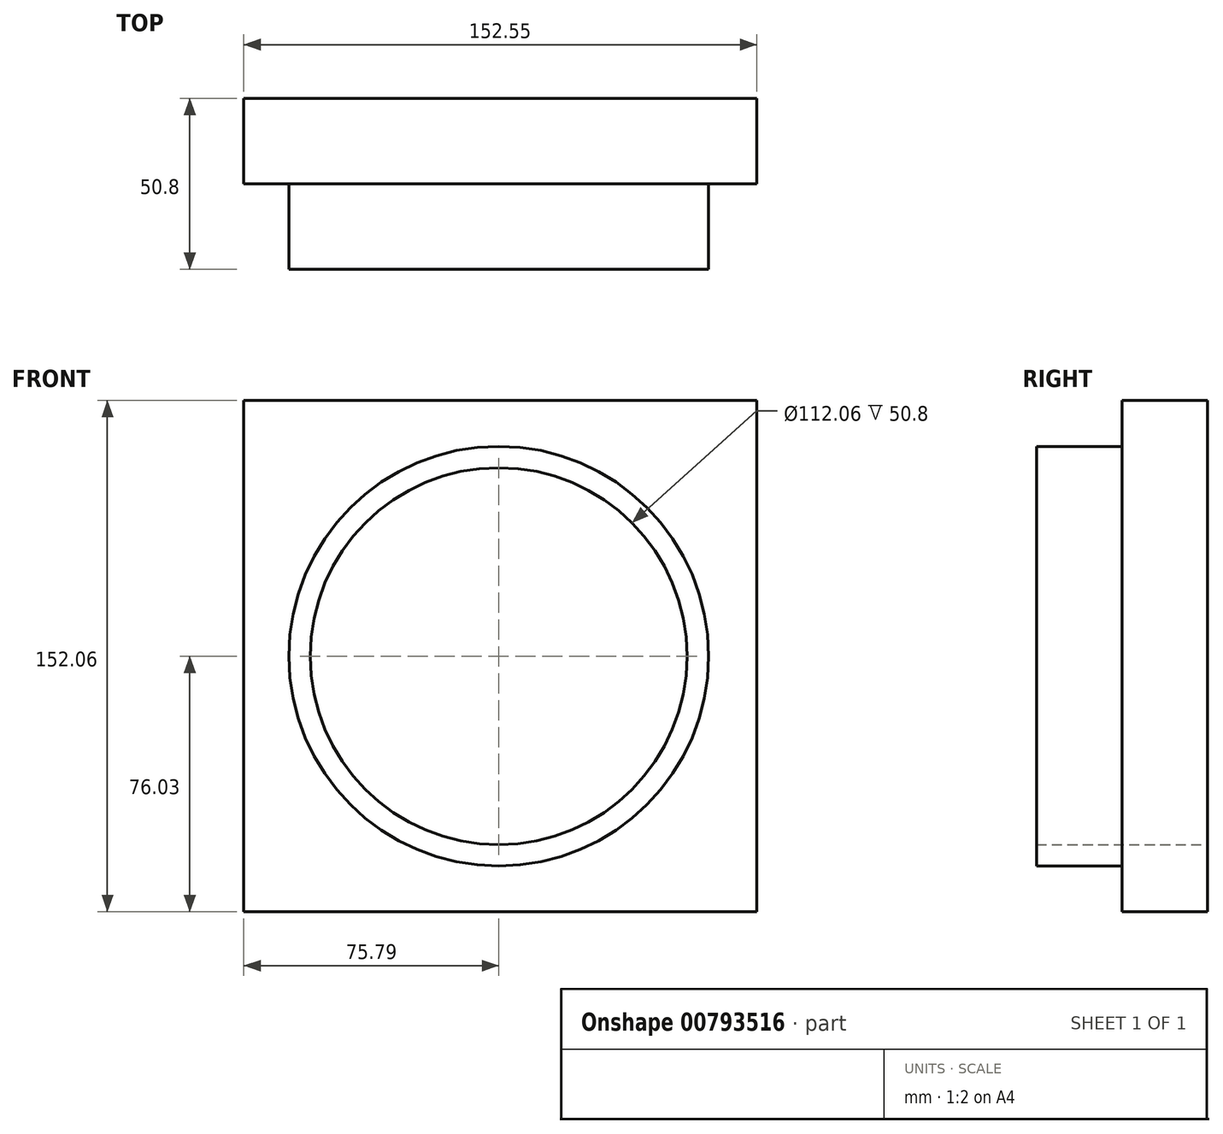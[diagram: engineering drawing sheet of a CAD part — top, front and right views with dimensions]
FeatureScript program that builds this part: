
annotation { "Feature Type Name" : "Feature", "Feature Type Description" : "" }
export const myFeature = defineFeature(function(context is Context, id is Id, definition is map)
    precondition{}
    {
        {
            var Q0;
            Q0=qCreatedBy(makeId("Front.planeOp"),FACE);
            var sketch = newSketch(context, id + "F0", { "sketchPlane" : qUnion([Q0])});
            skCircle(sketch, "E0", {"center": v(0, 0) * mm, "radius": 56.03 * mm});
            skLineSegment(sketch, "E1.bottom", {"start": v(-75.8, 76.03) * mm, "end": v(76.76, 76.03) * mm});
            skLineSegment(sketch, "E1.top", {"start": v(-75.8, -76.03) * mm, "end": v(76.76, -76.03) * mm});
            skLineSegment(sketch, "E1.left", {"start": v(-75.8, 76.03) * mm, "end": v(-75.8, -76.03) * mm});
            skLineSegment(sketch, "E1.right", {"start": v(76.76, 76.03) * mm, "end": v(76.76, -76.03) * mm});
            skCircle(sketch, "E2.0", {"center": v(0, 0) * mm, "radius": 62.38 * mm});
            skSolve(sketch);
        }
        {
            var Q0;
            Q0=makeQuery(id+"F0.imprint","IMPRINT",FACE,{"disambiguationData":[TD([[makeQuery(id+"F0.imprint","IMPRINT",EDGE,{"derivedFrom":sQuery(id+"F0.wireOp",EDGE,"E1.bottom")}),-1.0]])]});
            extrude(context, id + "F1", {"entities" : qUnion([Q0]), "depth" : 25.4 * mm, "offsetDistance" : 25.4 * mm});
        }
        {
            var Q0;
            Q0=makeQuery(id+"F0.imprint","IMPRINT",FACE,{"disambiguationData":[TD([[makeQuery(id+"F0.imprint","IMPRINT",EDGE,{"derivedFrom":sQuery(id+"F0.wireOp",EDGE,"E0")}),-1.0]])]});
            extrude(context, id + "F2", {"entities" : qUnion([Q0]), "operationType" : NewBodyOperationType.ADD, "depth" : 50.8 * mm, "offsetDistance" : 25.4 * mm});
        }
    });
